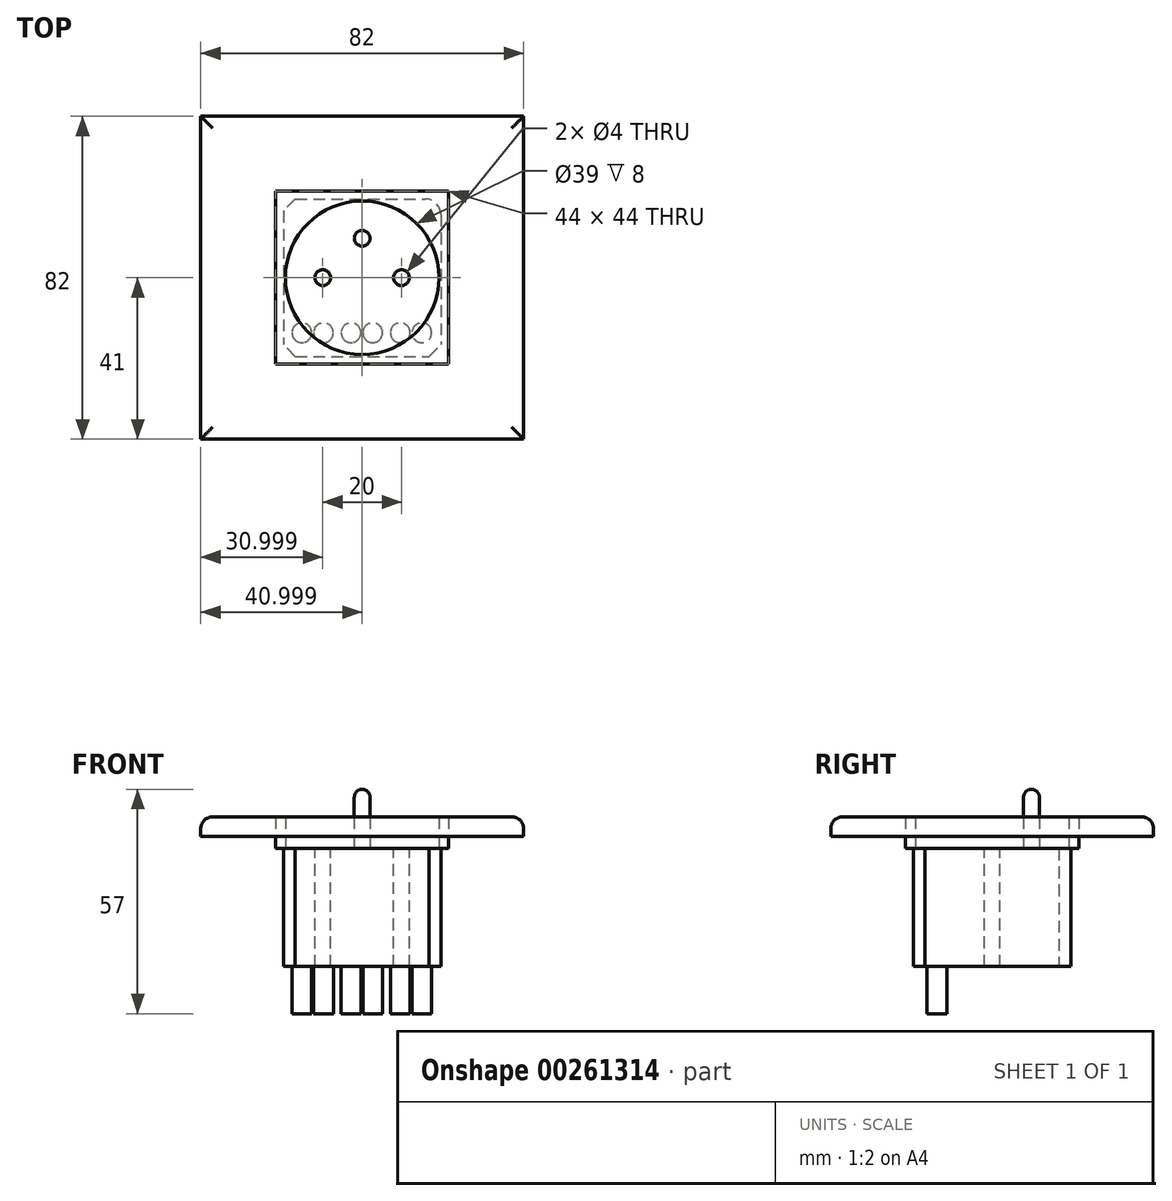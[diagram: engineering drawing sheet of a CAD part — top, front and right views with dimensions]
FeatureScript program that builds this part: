
annotation { "Feature Type Name" : "Feature", "Feature Type Description" : "" }
export const myFeature = defineFeature(function(context is Context, id is Id, definition is map)
    precondition{}
    {
        {
            var Q0;
            Q0=qCreatedBy(makeId("Top.planeOp"),FACE);
            var sketch = newSketch(context, id + "F0", { "sketchPlane" : qUnion([Q0])});
            skLineSegment(sketch, "E0.bottom", {"start": v(-21.61, -17.92) * mm, "end": v(22.39, -17.92) * mm});
            skLineSegment(sketch, "E0.top", {"start": v(-21.61, 26.08) * mm, "end": v(22.39, 26.08) * mm});
            skLineSegment(sketch, "E0.left", {"start": v(-21.61, -17.92) * mm, "end": v(-21.61, 26.08) * mm});
            skLineSegment(sketch, "E0.right", {"start": v(22.39, -17.92) * mm, "end": v(22.39, 26.08) * mm});
            skLineSegment(sketch, "E1.bottom", {"start": v(-19.61, 24.08) * mm, "end": v(20.39, 24.08) * mm});
            skLineSegment(sketch, "E1.top", {"start": v(-19.61, -15.92) * mm, "end": v(20.39, -15.92) * mm});
            skLineSegment(sketch, "E1.left", {"start": v(-19.61, 24.08) * mm, "end": v(-19.61, -15.92) * mm});
            skLineSegment(sketch, "E1.right", {"start": v(20.39, 24.08) * mm, "end": v(20.39, -15.92) * mm});
            skLineSegment(sketch, "E2", {"start": v(-19.61, 4.08) * mm, "end": v(20.39, 4.08) * mm, "construction": true});
            skCircle(sketch, "E3", {"center": v(-9.61, 4.08) * mm, "radius": 2 * mm});
            skCircle(sketch, "E4", {"center": v(10.39, 4.08) * mm, "radius": 2 * mm});
            skLineSegment(sketch, "E5", {"start": v(0.39, 24.08) * mm, "end": v(0.39, -15.92) * mm, "construction": true});
            skLineSegment(sketch, "E6", {"start": v(-19.61, 24.08) * mm, "end": v(20.39, 4.08) * mm, "construction": true});
            skPoint(sketch, "E7.centerSnap0", {"position": v(0.39, 14.08) * mm});
            skCircle(sketch, "E8", {"center": v(0.39, 14.08) * mm, "radius": 2 * mm});
            skCircle(sketch, "E9", {"center": v(0.39, 4.08) * mm, "radius": 19.5 * mm});
            skLineSegment(sketch, "E10", {"start": v(6.56, 24.08) * mm, "end": v(6.56, 26.08) * mm, "construction": true});
            skLineSegment(sketch, "E11", {"start": v(6.56, -15.92) * mm, "end": v(6.56, -17.92) * mm, "construction": true});
            skLineSegment(sketch, "E12", {"start": v(22.39, -8.42) * mm, "end": v(20.39, -8.42) * mm, "construction": true});
            skLineSegment(sketch, "E13", {"start": v(-19.61, -8.42) * mm, "end": v(-21.61, -8.42) * mm, "construction": true});
            skSolve(sketch);
        }
        {
            var Q0;
            Q0=makeQuery(id+"F0.imprint","IMPRINT",FACE,{"disambiguationData":[TD([[makeQuery(id+"F0.imprint","IMPRINT",EDGE,{"derivedFrom":sQuery(id+"F0.wireOp",EDGE,"E1.bottom")}),-1.0]])]});
            var Q1;
            Q1=makeQuery(id+"F0.imprint","IMPRINT",FACE,{"disambiguationData":[TD([[makeQuery(id+"F0.imprint","IMPRINT",EDGE,{"derivedFrom":sQuery(id+"F0.wireOp",EDGE,"E0.bottom")}),1.0]])]});
            extrude(context, id + "F1", {"entities" : qUnion([Q0, Q1]), "depth" : 8 * mm});
        }
        {
            var Q0;
            Q0=makeQuery(id+"F0.imprint","IMPRINT",FACE,{"disambiguationData":[TD([[makeQuery(id+"F0.imprint","IMPRINT",EDGE,{"derivedFrom":sQuery(id+"F0.wireOp",EDGE,"E1.bottom")}),-1.0]])]});
            var Q1;
            Q1=makeQuery(id+"F0.imprint","IMPRINT",FACE,{"disambiguationData":[TD([[makeQuery(id+"F0.imprint","IMPRINT",EDGE,{"derivedFrom":sQuery(id+"F0.wireOp",EDGE,"E3")}),-1.0]])]});
            var Q2;
            Q2=makeQuery(id+"F0.imprint","IMPRINT",FACE,{"disambiguationData":[TD([[makeQuery(id+"F0.imprint","IMPRINT",EDGE,{"derivedFrom":sQuery(id+"F0.wireOp",EDGE,"E8")}),1.0]])]});
            extrude(context, id + "F2", {"entities" : qUnion([Q0, Q1, Q2]), "operationType" : NewBodyOperationType.ADD, "oppositeDirection" : true, "depth" : 30 * mm});
        }
        {
            var Q0;
            Q0=makeQuery(id+"F0.imprint","IMPRINT",FACE,{"disambiguationData":[TD([[makeQuery(id+"F0.imprint","IMPRINT",EDGE,{"derivedFrom":sQuery(id+"F0.wireOp",EDGE,"E8")}),1.0]])]});
            extrude(context, id + "F3", {"entities" : qUnion([Q0]), "operationType" : NewBodyOperationType.ADD, "depth" : 15 * mm});
        }
        {
            var Q0;
            Q0=makeQuery(id+"F3.opExtrude","CAP_EDGE",EDGE,{"disambiguationData":[OSD([sQuery(id+"F0.wireOp",EDGE,"E8")])],"isStart":false});
            fillet(context, id + "F4", {"entities" : qUnion([Q0]), "radius" : 2 * mm, "tangentPropagation" : true, "allowEdgeOverflow" : false});
        }
        {
            var Q0;
            Q0=makeQuery(id+"F1.opExtrude","CAP_FACE",FACE,{"disambiguationData":[OSD([sQuery(id+"F0.wireOp",EDGE,"E0.bottom"),sQuery(id+"F0.wireOp",EDGE,"E0.top"),sQuery(id+"F0.wireOp",EDGE,"E0.left"),sQuery(id+"F0.wireOp",EDGE,"E0.right"),sQuery(id+"F0.wireOp",EDGE,"E9")])],"isStart":false});
            var sketch = newSketch(context, id + "F5", { "sketchPlane" : qUnion([Q0])});
            skLineSegment(sketch, "E14.bottom", {"start": v(-40.61, 45.08) * mm, "end": v(41.39, 45.08) * mm});
            skLineSegment(sketch, "E14.top", {"start": v(-40.61, -36.92) * mm, "end": v(41.39, -36.92) * mm});
            skLineSegment(sketch, "E14.left", {"start": v(-40.61, 45.08) * mm, "end": v(-40.61, -36.92) * mm});
            skLineSegment(sketch, "E14.right", {"start": v(41.39, 45.08) * mm, "end": v(41.39, -36.92) * mm});
            skLineSegment(sketch, "E15", {"start": v(-40.61, 45.08) * mm, "end": v(41.39, -36.92) * mm, "construction": true});
            skLineSegment(sketch, "E16", {"start": v(41.39, 45.08) * mm, "end": v(-40.61, -36.92) * mm, "construction": true});
            skSolve(sketch);
        }
        {
            var Q0;
            Q0=makeQuery(id+"F5.imprint","IMPRINT",FACE,{"disambiguationData":[TD([[makeQuery(id+"F5.imprint","IMPRINT",EDGE,{"derivedFrom":sQuery(id+"F5.wireOp",EDGE,"E14.bottom")}),-1.0]])]});
            extrude(context, id + "F6", {"entities" : qUnion([Q0]), "oppositeDirection" : true, "depth" : 5 * mm});
        }
        {
            var Q0;
            Q0=makeQuery(id+"F6.opExtrude","SWEPT_FACE",FACE,{"disambiguationData":[OSD([sQuery(id+"F5.wireOp",EDGE,"E14.left")])]});
            var sketch = newSketch(context, id + "F7", { "sketchPlane" : qUnion([Q0])});
            skLineSegment(sketch, "E17", {"start": v(33.92, 8) * mm, "end": v(33.92, 5) * mm, "construction": true});
            skLineSegment(sketch, "E18", {"start": v(33.92, 5) * mm, "end": v(36.92, 5) * mm, "construction": true});
            skArc(sketch, "E19", {"start": v(36.92, 5) * mm, "mid": v(36.04, 7.12) * mm, "end": v(33.92, 8) * mm});
            skLineSegment(sketch, "E20", {"start": v(33.92, 8) * mm, "end": v(36.92, 8) * mm});
            skLineSegment(sketch, "E21", {"start": v(36.92, 8) * mm, "end": v(36.92, 5) * mm});
            skLineSegment(sketch, "E22", {"start": v(-45.08, 5) * mm, "end": v(-42.08, 5) * mm, "construction": true});
            skLineSegment(sketch, "E23", {"start": v(-42.08, 5) * mm, "end": v(-42.08, 8) * mm, "construction": true});
            skArc(sketch, "E24", {"start": v(-42.08, 8) * mm, "mid": v(-44.2, 7.12) * mm, "end": v(-45.08, 5) * mm});
            skLineSegment(sketch, "E25", {"start": v(-42.08, 8) * mm, "end": v(-45.08, 8) * mm});
            skLineSegment(sketch, "E26", {"start": v(-45.08, 8) * mm, "end": v(-45.08, 5) * mm});
            skSolve(sketch);
        }
        {
            var Q0;
            Q0=makeQuery(id+"F6.opExtrude","SWEPT_FACE",FACE,{"disambiguationData":[OSD([sQuery(id+"F5.wireOp",EDGE,"E14.top")])]});
            var sketch = newSketch(context, id + "F8", { "sketchPlane" : qUnion([Q0])});
            skLineSegment(sketch, "E27", {"start": v(-37.61, 8) * mm, "end": v(-37.61, 5) * mm, "construction": true});
            skLineSegment(sketch, "E28", {"start": v(-37.61, 5) * mm, "end": v(-40.61, 5) * mm, "construction": true});
            skArc(sketch, "E29", {"start": v(-37.61, 8) * mm, "mid": v(-39.73, 7.12) * mm, "end": v(-40.61, 5) * mm});
            skLineSegment(sketch, "E30", {"start": v(-37.61, 8) * mm, "end": v(-40.61, 8) * mm});
            skLineSegment(sketch, "E31", {"start": v(-40.61, 8) * mm, "end": v(-40.61, 5) * mm});
            skLineSegment(sketch, "E32", {"start": v(38.39, 5) * mm, "end": v(38.39, 8) * mm, "construction": true});
            skLineSegment(sketch, "E33", {"start": v(38.39, 5) * mm, "end": v(41.39, 5) * mm, "construction": true});
            skArc(sketch, "E34", {"start": v(41.39, 5) * mm, "mid": v(40.51, 7.12) * mm, "end": v(38.39, 8) * mm});
            skLineSegment(sketch, "E35", {"start": v(38.39, 8) * mm, "end": v(41.39, 8) * mm});
            skLineSegment(sketch, "E36", {"start": v(41.39, 8) * mm, "end": v(41.39, 5) * mm});
            skSolve(sketch);
        }
        {
            var Q0;
            Q0=makeQuery(id+"F7.imprint","IMPRINT",FACE,{"disambiguationData":[TD([[makeQuery(id+"F7.imprint","IMPRINT",EDGE,{"derivedFrom":sQuery(id+"F7.wireOp",EDGE,"E24")}),-1.0]])]});
            var Q1;
            Q1=makeQuery(id+"F7.imprint","IMPRINT",FACE,{"disambiguationData":[TD([[makeQuery(id+"F7.imprint","IMPRINT",EDGE,{"derivedFrom":sQuery(id+"F7.wireOp",EDGE,"E19")}),-1.0]])]});
            extrude(context, id + "F9", {"entities" : qUnion([Q0, Q1]), "operationType" : NewBodyOperationType.REMOVE, "endBound" : BoundingType.THROUGH_ALL, "oppositeDirection" : true, "depth" : 25 * mm});
        }
        {
            var Q0;
            Q0=makeQuery(id+"F8.imprint","IMPRINT",FACE,{"disambiguationData":[TD([[makeQuery(id+"F8.imprint","IMPRINT",EDGE,{"derivedFrom":sQuery(id+"F8.wireOp",EDGE,"E34")}),-1.0]])]});
            var Q1;
            Q1=makeQuery(id+"F8.imprint","IMPRINT",FACE,{"disambiguationData":[TD([[makeQuery(id+"F8.imprint","IMPRINT",EDGE,{"derivedFrom":sQuery(id+"F8.wireOp",EDGE,"E29")}),-1.0]])]});
            extrude(context, id + "F10", {"entities" : qUnion([Q0, Q1]), "operationType" : NewBodyOperationType.REMOVE, "endBound" : BoundingType.THROUGH_ALL, "oppositeDirection" : true, "depth" : 25 * mm});
        }
        {
            var Q0;
            Q0=makeQuery(id+"F2.opExtrude","SWEPT_EDGE",EDGE,{"disambiguationData":[OSD([sQuery(id+"F0.wireOp",EDGE,"E1.bottom"),sQuery(id+"F0.wireOp",EDGE,"E1.right")])]});
            fillet(context, id + "F11", {"entities" : qUnion([Q0]), "radius" : 4 * mm, "tangentPropagation" : true, "allowEdgeOverflow" : false});
        }
        {
            var Q0;
            Q0=makeQuery(id+"F2.opExtrude","SWEPT_EDGE",EDGE,{"disambiguationData":[OSD([sQuery(id+"F0.wireOp",EDGE,"E1.bottom"),sQuery(id+"F0.wireOp",EDGE,"E1.right")])]});
            var Q1;
            Q1=makeQuery(id+"F2.opExtrude","SWEPT_EDGE",EDGE,{"disambiguationData":[OSD([sQuery(id+"F0.wireOp",EDGE,"E1.bottom"),sQuery(id+"F0.wireOp",EDGE,"E1.left")])]});
            var Q2;
            Q2=makeQuery(id+"F2.opExtrude","SWEPT_EDGE",EDGE,{"disambiguationData":[OSD([sQuery(id+"F0.wireOp",EDGE,"E1.top"),sQuery(id+"F0.wireOp",EDGE,"E1.left")])]});
            var Q3;
            Q3=makeQuery(id+"F2.opExtrude","SWEPT_EDGE",EDGE,{"disambiguationData":[OSD([sQuery(id+"F0.wireOp",EDGE,"E1.top"),sQuery(id+"F0.wireOp",EDGE,"E1.right")])]});
            chamfer(context, id + "F12", {"entities" : qUnion([Q0, Q1, Q2, Q3]), "width" : 3 * mm, "tangentPropagation" : true});
        }
        {
            var Q0;
            Q0=makeQuery(id+"F2.opExtrude","CAP_FACE",FACE,{"disambiguationData":[OSD([sQuery(id+"F0.wireOp",EDGE,"E1.bottom"),sQuery(id+"F0.wireOp",EDGE,"E1.top"),sQuery(id+"F0.wireOp",EDGE,"E1.left"),sQuery(id+"F0.wireOp",EDGE,"E1.right"),sQuery(id+"F0.wireOp",EDGE,"E3"),sQuery(id+"F0.wireOp",EDGE,"E4")])],"isStart":false});
            var sketch = newSketch(context, id + "F13", { "sketchPlane" : qUnion([Q0])});
            skCircle(sketch, "E37", {"center": v(15.56, 9.92) * mm, "radius": 2.5 * mm});
            skLineSegment(sketch, "E38", {"start": v(15.56, 9.92) * mm, "end": v(-16.77, 9.92) * mm, "construction": true});
            skCircle(sketch, "E39", {"center": v(10.06, 9.92) * mm, "radius": 2.5 * mm});
            skCircle(sketch, "E40.1.0.0", {"center": v(3.06, 9.92) * mm, "radius": 2.5 * mm});
            skCircle(sketch, "E40.1.0.1", {"center": v(-2.44, 9.92) * mm, "radius": 2.5 * mm});
            skCircle(sketch, "E40.2.0.0", {"center": v(-9.44, 9.92) * mm, "radius": 2.5 * mm});
            skCircle(sketch, "E40.2.0.1", {"center": v(-14.94, 9.92) * mm, "radius": 2.5 * mm});
            skLineSegment(sketch, "E40.direction1", {"start": v(15.56, 9.92) * mm, "end": v(3.06, 9.92) * mm, "construction": true});
            skSolve(sketch);
        }
        {
            var Q0;
            Q0=makeQuery(id+"F13.imprint","IMPRINT",FACE,{"disambiguationData":[TD([[makeQuery(id+"F13.imprint","IMPRINT",EDGE,{"derivedFrom":sQuery(id+"F13.wireOp",EDGE,"E39")}),1.0]])]});
            var Q1;
            Q1=makeQuery(id+"F13.imprint","IMPRINT",FACE,{"disambiguationData":[TD([[makeQuery(id+"F13.imprint","IMPRINT",EDGE,{"derivedFrom":sQuery(id+"F13.wireOp",EDGE,"E40.1.0.0")}),1.0]])]});
            var Q2;
            Q2=makeQuery(id+"F13.imprint","IMPRINT",FACE,{"disambiguationData":[TD([[makeQuery(id+"F13.imprint","IMPRINT",EDGE,{"derivedFrom":sQuery(id+"F13.wireOp",EDGE,"E37")}),1.0]])]});
            var Q3;
            Q3=makeQuery(id+"F13.imprint","IMPRINT",FACE,{"disambiguationData":[TD([[makeQuery(id+"F13.imprint","IMPRINT",EDGE,{"derivedFrom":sQuery(id+"F13.wireOp",EDGE,"E40.1.0.1")}),1.0]])]});
            var Q4;
            Q4=makeQuery(id+"F13.imprint","IMPRINT",FACE,{"disambiguationData":[TD([[makeQuery(id+"F13.imprint","IMPRINT",EDGE,{"derivedFrom":sQuery(id+"F13.wireOp",EDGE,"E40.2.0.0")}),1.0]])]});
            var Q5;
            Q5=makeQuery(id+"F13.imprint","IMPRINT",FACE,{"disambiguationData":[TD([[makeQuery(id+"F13.imprint","IMPRINT",EDGE,{"derivedFrom":sQuery(id+"F13.wireOp",EDGE,"E40.2.0.1")}),1.0]])]});
            extrude(context, id + "F14", {"entities" : qUnion([Q0, Q1, Q2, Q3, Q4, Q5]), "operationType" : NewBodyOperationType.ADD, "depth" : 12 * mm});
        }
    });
